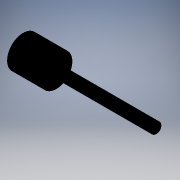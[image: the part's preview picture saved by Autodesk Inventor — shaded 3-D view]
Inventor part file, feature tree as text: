
AUTODESK INVENTOR PART (.ipt)
format: ipt  version: 2017.3 (Build 213256000, 256)  size: 140,288 bytes
history: native  units: mm (DEFAULTED — no unit token found)
features: other x70, revolve x3, sketch x3
ambient origin geometry x8: Origin, YZ Plane, XZ Plane, XY Plane, X Axis, Y Axis, Z Axis, Center Point
bodies: Solid1 (feature_tree)
feature tree (76):
  revolve  "Revolution1"  Angle=360.0deg
  revolve  "Revolution2"  [1 undecoded]
  revolve  "Revolution3"  [1 undecoded]
  other  "dia1_XY"
  other  "dia1_YZ"
  other  "dia1_ZX"
  other  "dia1_X"
  other  "dia1_Y"
  other  "dia1_Z"
  other  "dia1_Center"
  other  "dia12_XY"
  other  "dia12_YZ"
  other  "dia12_ZX"
  other  "dia12_X"
  other  "dia12_Y"
  other  "dia12_Z"
  other  "dia12_Center"
  other  "dia2_XY"
  other  "dia2_YZ"
  other  "dia2_ZX"
  other  "dia2_X"
  other  "dia2_Y"
  other  "dia2_Z"
  other  "dia2_Center"
  other  "dia22_XY"
  other  "dia22_YZ"
  other  "dia22_ZX"
  other  "dia22_X"
  other  "dia22_Y"
  other  "dia22_Z"
  other  "dia22_Center"
  other  "rl1_XY"
  other  "rl1_YZ"
  other  "rl1_ZX"
  other  "rl1_X"
  other  "rl1_Y"
  other  "rl1_Z"
  other  "rl1_Center"
  other  "rl2_XY"
  other  "rl2_YZ"
  other  "rl2_ZX"
  other  "rl2_X"
  other  "rl2_Y"
  other  "rl2_Z"
  other  "rl2_Center"
  other  "rod_cp_XY"
  other  "rod_cp_YZ"
  other  "rod_cp_ZX"
  other  "rod_cp_X"
  other  "rod_cp_Y"
  other  "rod_cp_Z"
  other  "rod_cp_Center"
  other  "thd1_XY"
  other  "thd1_YZ"
  other  "thd1_ZX"
  other  "thd1_X"
  other  "thd1_Y"
  other  "thd1_Z"
  other  "thd1_Center"
  other  "thd2_XY"
  other  "thd2_YZ"
  other  "thd2_ZX"
  other  "thd2_X"
  other  "thd2_Y"
  other  "thd2_Z"
  other  "thd2_Center"
  other  "to_rod_clevis_XY"
  other  "to_rod_clevis_YZ"
  other  "to_rod_clevis_ZX"
  other  "to_rod_clevis_X"
  other  "to_rod_clevis_Y"
  other  "to_rod_clevis_Z"
  other  "to_rod_clevis_Center"
  sketch  "Sketch_1"  dims[d0=360.0deg d1=360.0deg]
  sketch  "Sketch_3"  dims[d2=360.0deg]
  sketch  "Sketch_30"  dims[d3=0.0mm d4=0.0mm d5=0.0mm d6=0.0mm d7=0.0mm]
note: 2 required parameter values undecoded (feature->parameter linkage not recoverable at this tier; creation-order binding heuristic only, values carry confidence <= 0.55)
